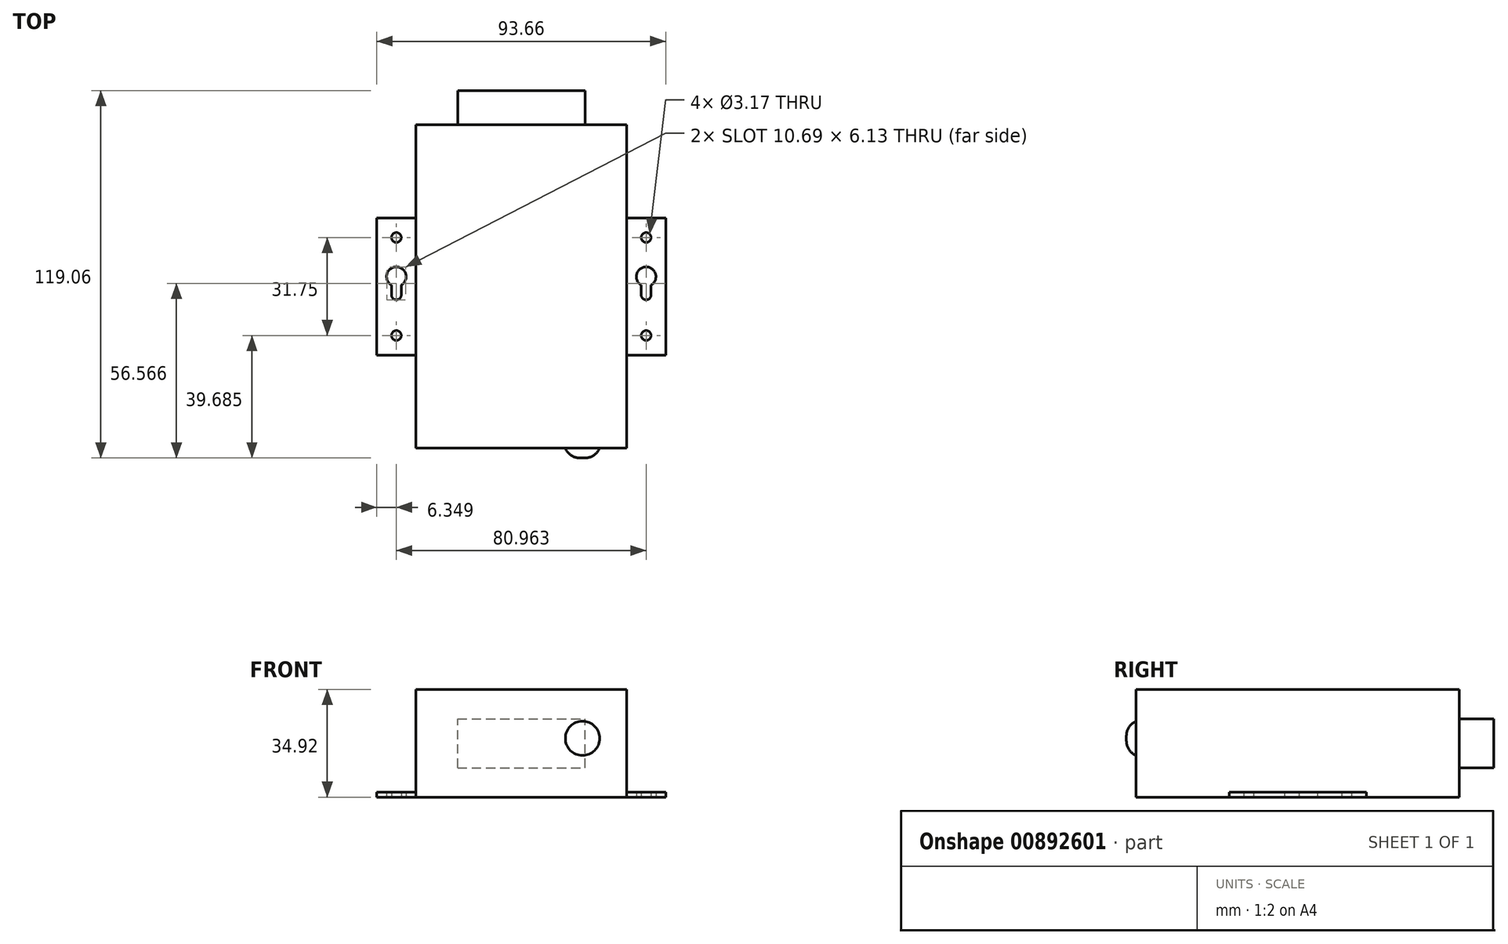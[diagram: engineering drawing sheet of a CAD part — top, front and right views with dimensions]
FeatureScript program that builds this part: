
annotation { "Feature Type Name" : "Feature", "Feature Type Description" : "" }
export const myFeature = defineFeature(function(context is Context, id is Id, definition is map)
    precondition{}
    {
        {
            var Q0;
            Q0=qCreatedBy(makeId("Top.planeOp"),FACE);
            var sketch = newSketch(context, id + "F0", { "sketchPlane" : qUnion([Q0])});
            skLineSegment(sketch, "E0.bottom", {"start": v(34.13, 52.39) * mm, "end": v(-34.13, 52.39) * mm});
            skLineSegment(sketch, "E0.top", {"start": v(34.13, -52.39) * mm, "end": v(-34.13, -52.39) * mm});
            skLineSegment(sketch, "E0.left", {"start": v(34.13, 52.39) * mm, "end": v(34.13, -52.39) * mm});
            skLineSegment(sketch, "E0.right", {"start": v(-34.13, 52.39) * mm, "end": v(-34.13, -52.39) * mm});
            skPoint(sketch, "E0.middle", {"position": v(0, 0) * mm});
            skLineSegment(sketch, "E1.bottom", {"start": v(34.13, 22.23) * mm, "end": v(46.83, 22.23) * mm});
            skLineSegment(sketch, "E1.top", {"start": v(34.13, -22.22) * mm, "end": v(46.83, -22.22) * mm});
            skLineSegment(sketch, "E1.left", {"start": v(34.13, 22.23) * mm, "end": v(34.13, -22.22) * mm});
            skLineSegment(sketch, "E1.right", {"start": v(46.83, 22.23) * mm, "end": v(46.83, -22.22) * mm});
            skPoint(sketch, "E1.middle", {"position": v(40.48, 0) * mm});
            skPoint(sketch, "E1.middle.positionSnap0", {"position": v(34.13, 0) * mm});
            skPoint(sketch, "E1.centerSnap0", {"position": v(34.13, 0) * mm});
            skLineSegment(sketch, "E2.bottom", {"start": v(-46.83, 22.23) * mm, "end": v(-34.13, 22.23) * mm});
            skLineSegment(sketch, "E2.top", {"start": v(-46.83, -22.22) * mm, "end": v(-34.13, -22.22) * mm});
            skLineSegment(sketch, "E2.left", {"start": v(-46.83, 22.23) * mm, "end": v(-46.83, -22.22) * mm});
            skLineSegment(sketch, "E2.right", {"start": v(-34.13, 22.23) * mm, "end": v(-34.13, -22.22) * mm});
            skPoint(sketch, "E2.middle", {"position": v(-40.48, 0) * mm});
            skArc(sketch, "E3", {"start": v(42.07, 0.43) * mm, "mid": v(40.48, 6.35) * mm, "end": v(38.9, 0.43) * mm});
            skArc(sketch, "E4", {"start": v(38.9, -2.75) * mm, "mid": v(40.48, -4.34) * mm, "end": v(42.07, -2.75) * mm});
            skCircle(sketch, "E5", {"center": v(40.48, -15.87) * mm, "radius": 1.59 * mm});
            skCircle(sketch, "E6", {"center": v(40.48, 15.88) * mm, "radius": 1.59 * mm});
            skLineSegment(sketch, "E7", {"start": v(38.9, -2.75) * mm, "end": v(38.9, 0.43) * mm});
            skLineSegment(sketch, "E8", {"start": v(42.07, -2.75) * mm, "end": v(42.07, 0.43) * mm});
            skLineSegment(sketch, "E9.MirrorCS", {"start": v(-38.9, -2.75) * mm, "end": v(-38.9, 0.43) * mm});
            skCircle(sketch, "E10.MirrorC", {"center": v(-40.48, -15.87) * mm, "radius": 1.59 * mm});
            skLineSegment(sketch, "E11.MirrorCS", {"start": v(-42.07, -2.75) * mm, "end": v(-42.07, 0.43) * mm});
            skArc(sketch, "E12.MirrorCS", {"start": v(-38.9, -2.75) * mm, "mid": v(-40.48, -4.34) * mm, "end": v(-42.07, -2.75) * mm});
            skArc(sketch, "E13.MirrorCS", {"start": v(-42.07, 0.43) * mm, "mid": v(-40.48, 6.35) * mm, "end": v(-38.9, 0.43) * mm});
            skCircle(sketch, "E14.MirrorC", {"center": v(-40.48, 15.88) * mm, "radius": 1.59 * mm});
            skSolve(sketch);
        }
        {
            var Q0;
            {var subQ4=sQuery(id+"F0.wireOp",EDGE,"E0.bottom");Q0=makeQuery(id+"F0.imprint","IMPRINT",FACE,{"disambiguationData":[TD([[makeQuery(id+"F0.imprint","IMPRINT",EDGE,{"derivedFrom":subQ4}),1.0]])]});}
            extrude(context, id + "F1", {"entities" : qUnion([Q0]), "depth" : 34.92 * mm, "offsetDistance" : 25.4 * mm});
        }
        {
            var Q0;
            {var subQ1=sQuery(id+"F0.wireOp",EDGE,"E2.bottom");Q0=makeQuery(id+"F0.imprint","IMPRINT",FACE,{"disambiguationData":[TD([[makeQuery(id+"F0.imprint","IMPRINT",EDGE,{"derivedFrom":subQ1}),-1.0]])]});}
            var Q1;
            {var subQ1=sQuery(id+"F0.wireOp",EDGE,"E1.bottom");Q1=makeQuery(id+"F0.imprint","IMPRINT",FACE,{"disambiguationData":[TD([[makeQuery(id+"F0.imprint","IMPRINT",EDGE,{"derivedFrom":subQ1}),-1.0]])]});}
            extrude(context, id + "F2", {"entities" : qUnion([Q0, Q1]), "operationType" : NewBodyOperationType.ADD, "depth" : 1.59 * mm, "offsetDistance" : 25.4 * mm});
        }
        {
            var Q0;
            Q0=makeQuery(id+"F1.opExtrude","SWEPT_FACE",FACE,{"disambiguationData":[OSD([sQuery(id+"F0.wireOp",EDGE,"E0.bottom")])]});
            var sketch = newSketch(context, id + "F3", { "sketchPlane" : qUnion([Q0])});
            skLineSegment(sketch, "E15.bottom", {"start": v(20.64, 9.53) * mm, "end": v(-20.64, 9.53) * mm});
            skLineSegment(sketch, "E15.top", {"start": v(20.64, 25.4) * mm, "end": v(-20.64, 25.4) * mm});
            skLineSegment(sketch, "E15.left", {"start": v(20.64, 9.53) * mm, "end": v(20.64, 25.4) * mm});
            skLineSegment(sketch, "E15.right", {"start": v(-20.64, 9.53) * mm, "end": v(-20.64, 25.4) * mm});
            skPoint(sketch, "E15.middle", {"position": v(0, 17.46) * mm});
            skSolve(sketch);
        }
        {
            var Q0;
            Q0 = qSketchRegion(id + "F3", true);
            extrude(context, id + "F4", {"entities" : qUnion([Q0]), "operationType" : NewBodyOperationType.ADD, "depth" : 11.1 * mm, "offsetDistance" : 25.4 * mm});
        }
        {
            var Q0;
            Q0=makeQuery(id+"F1.opExtrude","SWEPT_FACE",FACE,{"disambiguationData":[OSD([sQuery(id+"F0.wireOp",EDGE,"E0.top")])]});
            var sketch = newSketch(context, id + "F5", { "sketchPlane" : qUnion([Q0])});
            skCircle(sketch, "E16", {"center": v(19.84, 19.05) * mm, "radius": 5.56 * mm});
            skSolve(sketch);
        }
        {
            var Q0;
            Q0 = qSketchRegion(id + "F5", true);
            extrude(context, id + "F6", {"entities" : qUnion([Q0]), "operationType" : NewBodyOperationType.ADD, "depth" : 3.17 * mm, "offsetDistance" : 25.4 * mm});
        }
        {
            var Q0;
            Q0=makeQuery(id+"F6.opExtrude","CAP_FACE",FACE,{"disambiguationData":[OSD([sQuery(id+"F5.wireOp",EDGE,"E16")])],"isStart":false});
            fillet(context, id + "F7", {"entities" : qUnion([Q0]), "radius" : 5.08 * mm, "tangentPropagation" : true, "allowEdgeOverflow" : false});
        }
    });
